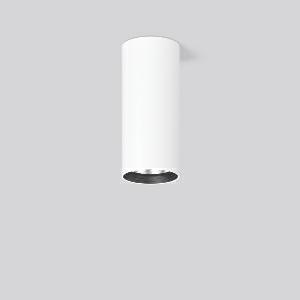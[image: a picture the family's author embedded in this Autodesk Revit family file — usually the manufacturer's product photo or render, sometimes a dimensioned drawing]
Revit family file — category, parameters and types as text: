
# Revit family: heledon_mini_a_931208_002_2_ae0f
name_source: partatom
category: Lighting Fixtures
units: mm (PartAtom-declared; Revit-internal decimal feet)

## family parameters
Cut with Voids When Loaded = No
Host = Face
Light Source = No
Part Type = Normal
Room Calculation Point = No
Round Connector Dimension = Use Diameter
Shared = No

## types (1)
- HELEDON mini A (1 x LED Modul 927, 3400 lm, 2700)
    Apparent Load = 29 VA
    Approval mark = CE
    CIE Flux Codes = 100 100 100 100 100
    Color Rendering = 92
    Color Temperature = 2700
    Default Elevation = 1800 mm
    Description = Series: HELEDON mini
Cylindrical surface-mounted downlight. Housing: die-cast aluminium, powder-coated. Internal ceiling frame polycarbonate with bayonet mounting. Black plastic ring and recessed LED to prevent glare from the side. Optical assembly with reflector made of MIRO-Silver with 98% total light reflection for outstanding efficiency - can be changed without tools. Best colour rendering index Ra>90. Suitable for Ceiling mounting. Easy installation with a separate ceiling frame with bayonet mounting and plug connection. Driver integrated. Connected via plug-in connector. High quality converter without flickering and stroboscopic effect. The following accessories can be mounted without use of tools: interchangeable lenses, decorative glasses, honeycomb louvre, clear and frosted diffusers, white interchangeable plastic ring. 
Colour: traffic white, matt (RAL 9016)
Diameter: 87 mm
Height: 197 mm
Lamp: LED
Socket: without socket
Colour temperature: 2700K
Colour rendering index (CRI): 92
System power: 29 W
Rated luminous flux: 3400 lm
Luminous efficiency: 117 lm/W
Control gear: Regulated power supply
Protection class: I
Type of protection: IP 20
    Height = 197 mm
    Lamp = 1 x LED Modul 927
    Lamp Light Flux = 3400 lm
    Lamp count = 1
    Length = 87 mm
    Lifetime = 50000 h
    Luminous efficacy = 117 lm/W
    Manufacturer = RZB
    ModVariant = No
    Model = 931208.002.2
    Mounting Place = Ceiling
    Mounting Type = Surface mounted
    Number of Poles = 1
    OnlyDefault = Yes
    Power Factor = 1
    Product Name = HELEDON mini A
    Product group = Surface mounted downlights
    ProductGroupID = 302
    Protection Class = Protection class I
    Protection Degree = IP 20
    RLX_Detail_Level = 1
    RLX_Emergency_Light_Flux = 0 lm
    RLX_Emergency_Type = 0
    RLX_Emergency_Type_DB = No
    RlxData = <blob elided: 107593 chars, md5=68789b84>
    Socket = socket
    Standby Power = 0 W
    System Light Flux = 3400 lm
    System Power = 29 W
    Type Comments = Product without accessories
    Type Image = 931188.002.jpg
    URL = http://relux.com
    VarID = ---
    Voltage = 230 V
    Voltage Range = 220-240 V
    Weight = 0.00 kg
    Width = 0 mm  [stored 0 ft]

note: [stored X ft] marks values corroborated as IEEE doubles in the binary element streams (Revit-internal decimal feet)

## geometry (parser evidence)
native form markers: Blend x4, Sweep x8
no freeform markers — native parametric forms only
